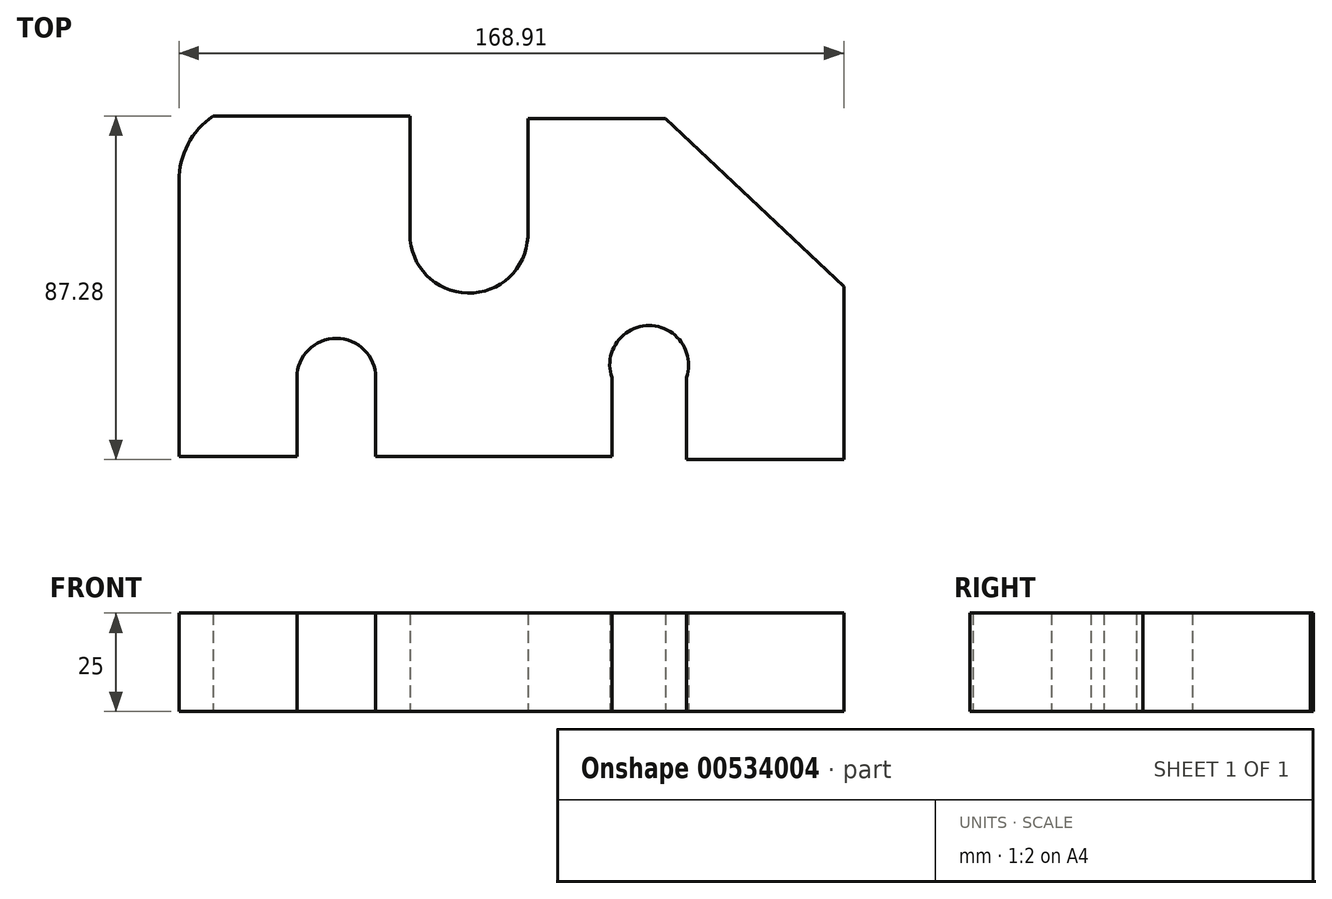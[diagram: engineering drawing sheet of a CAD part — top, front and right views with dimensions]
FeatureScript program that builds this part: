
annotation { "Feature Type Name" : "Feature", "Feature Type Description" : "" }
export const myFeature = defineFeature(function(context is Context, id is Id, definition is map)
    precondition{}
    {
        {
            var Q0;
            Q0=qCreatedBy(makeId("Top.planeOp"),FACE);
            var sketch = newSketch(context, id + "F0", { "sketchPlane" : qUnion([Q0])});
            skLineSegment(sketch, "E0", {"start": v(-64.17, -47.89) * mm, "end": v(-34.17, -47.89) * mm});
            skLineSegment(sketch, "E1", {"start": v(-34.17, -47.89) * mm, "end": v(-34.17, -27.89) * mm});
            skArc(sketch, "E2", {"start": v(-14.17, -27.89) * mm, "mid": v(-24.17, -17.89) * mm, "end": v(-34.17, -27.89) * mm});
            skLineSegment(sketch, "E3", {"start": v(-14.17, -27.89) * mm, "end": v(-14.17, -47.89) * mm});
            skLineSegment(sketch, "E4", {"start": v(-14.17, -47.89) * mm, "end": v(45.83, -47.89) * mm});
            skLineSegment(sketch, "E5", {"start": v(45.83, -47.89) * mm, "end": v(45.83, -27.89) * mm});
            skArc(sketch, "E6", {"start": v(64.74, -27.89) * mm, "mid": v(55.29, -14.64) * mm, "end": v(45.83, -27.89) * mm});
            skLineSegment(sketch, "E7", {"start": v(64.74, -27.89) * mm, "end": v(64.74, -48.69) * mm});
            skLineSegment(sketch, "E8", {"start": v(64.74, -48.69) * mm, "end": v(104.74, -48.69) * mm});
            skLineSegment(sketch, "E9", {"start": v(104.74, -48.69) * mm, "end": v(104.74, -4.69) * mm});
            skLineSegment(sketch, "E10", {"start": v(-64.17, -47.89) * mm, "end": v(-64.17, 22.11) * mm});
            skPoint(sketch, "E11.visualSharp", {"position": v(-64.17, 54.33) * mm});
            skArc(sketch, "E12", {"start": v(-55.5, 38.59) * mm, "mid": v(-61.87, 31.42) * mm, "end": v(-64.17, 22.11) * mm});
            skLineSegment(sketch, "E13", {"start": v(-55.5, 38.59) * mm, "end": v(-5.5, 38.59) * mm});
            skLineSegment(sketch, "E14", {"start": v(-5.5, 38.59) * mm, "end": v(-5.5, 8.59) * mm});
            skLineSegment(sketch, "E15", {"start": v(24.48, 37.9) * mm, "end": v(59.48, 37.9) * mm});
            skLineSegment(sketch, "E16", {"start": v(59.48, 37.9) * mm, "end": v(104.74, -4.69) * mm});
            skLineSegment(sketch, "E17", {"start": v(24.48, 37.9) * mm, "end": v(24.48, 7.9) * mm});
            skArc(sketch, "E18", {"start": v(-5.5, 8.59) * mm, "mid": v(9.14, -6.4) * mm, "end": v(24.48, 7.9) * mm});
            skSolve(sketch);
        }
        {
            var Q0;
            Q0 = qSketchRegion(id + "F0", true);
            extrude(context, id + "F1", {"entities" : qUnion([Q0]), "depth" : 25 * mm, "offsetDistance" : 25 * mm});
        }
    });
